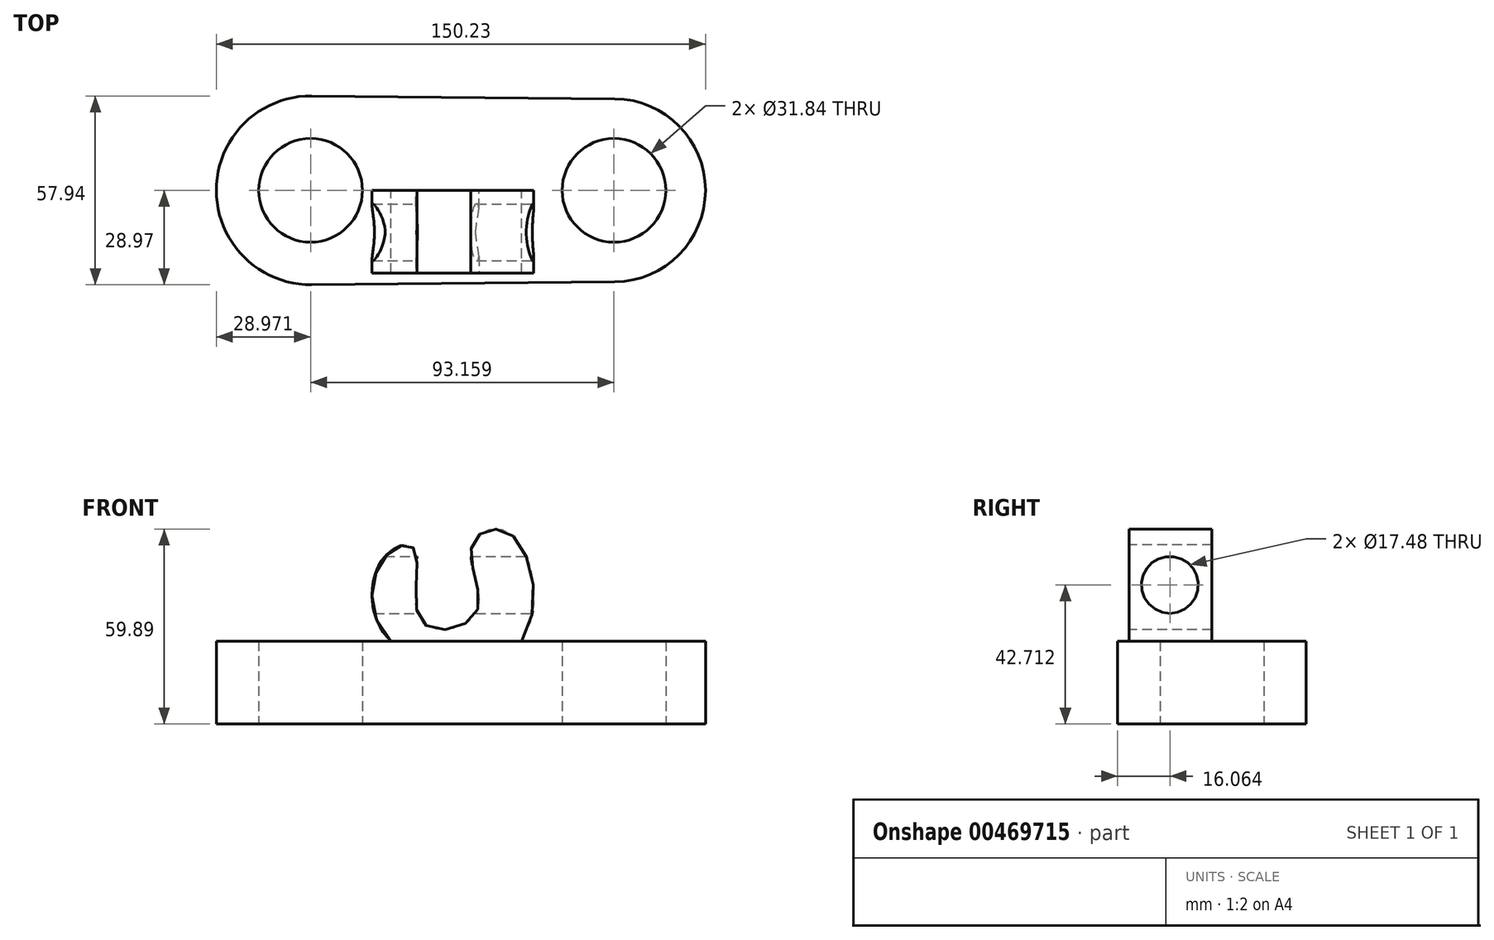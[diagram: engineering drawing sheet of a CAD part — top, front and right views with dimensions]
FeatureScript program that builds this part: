
annotation { "Feature Type Name" : "Feature", "Feature Type Description" : "" }
export const myFeature = defineFeature(function(context is Context, id is Id, definition is map)
    precondition{}
    {
        {
            var Q0;
            Q0=qCreatedBy(makeId("Top.planeOp"),FACE);
            var sketch = newSketch(context, id + "F0", { "sketchPlane" : qUnion([Q0])});
            skCircle(sketch, "E0", {"center": v(-46.58, 0) * mm, "radius": 15.92 * mm});
            skCircle(sketch, "E1", {"center": v(46.58, 0) * mm, "radius": 15.92 * mm});
            skArc(sketch, "E2", {"start": v(-46.3, 28.97) * mm, "mid": v(-75.55, 0) * mm, "end": v(-46.3, -28.97) * mm});
            skArc(sketch, "E3", {"start": v(46.84, -28.1) * mm, "mid": v(74.68, 0) * mm, "end": v(46.84, 28.1) * mm});
            skLineSegment(sketch, "E4", {"start": v(-46.3, 28.97) * mm, "end": v(46.84, 28.1) * mm});
            skLineSegment(sketch, "E5", {"start": v(46.84, -28.1) * mm, "end": v(-46.3, -28.97) * mm});
            skArc(sketch, "E6", {"start": v(-46.3, -28.97) * mm, "mid": v(-17.6, 0) * mm, "end": v(-46.3, 28.97) * mm});
            skSolve(sketch);
        }
        {
            var Q0;
            Q0=makeQuery(id+"F0.imprint","IMPRINT",FACE,{"disambiguationData":[TD([[makeQuery(id+"F0.imprint","IMPRINT",EDGE,{"derivedFrom":sQuery(id+"F0.wireOp",EDGE,"E0")}),-1.0]])]});
            extrude(context, id + "F1", {"entities" : qUnion([Q0]), "depth" : 25.4 * mm});
        }
        {
            var Q0;
            Q0=makeQuery(id+"F0.imprint","IMPRINT",FACE,{"disambiguationData":[TD([[makeQuery(id+"F0.imprint","IMPRINT",EDGE,{"derivedFrom":sQuery(id+"F0.wireOp",EDGE,"E1")}),-1.0]])]});
            extrude(context, id + "F2", {"entities" : qUnion([Q0]), "operationType" : NewBodyOperationType.ADD, "depth" : 25.4 * mm});
        }
        {
            var Q0;
            {var subQ0=sQuery(id+"F0.wireOp",EDGE,"E6");Q0=makeQuery(id+"F2.boolean.opBoolean","MERGE",FACE,{"derivedFrom":[makeQuery(id+"F1.opExtrude","CAP_FACE",FACE,{"disambiguationData":[OSD([sQuery(id+"F0.wireOp",EDGE,"E0"),sQuery(id+"F0.wireOp",EDGE,"E2"),subQ0])],"isStart":false}),makeQuery(id+"F2.opExtrude","CAP_FACE",FACE,{"disambiguationData":[OSD([sQuery(id+"F0.wireOp",EDGE,"E1"),sQuery(id+"F0.wireOp",EDGE,"E3"),sQuery(id+"F0.wireOp",EDGE,"E4"),sQuery(id+"F0.wireOp",EDGE,"E5"),subQ0])],"isStart":false})]});}
            var sketch = newSketch(context, id + "F3", { "sketchPlane" : qUnion([Q0])});
            skLineSegment(sketch, "E7", {"start": v(-21.34, -28.74) * mm, "end": v(-21.34, 28.74) * mm});
            skLineSegment(sketch, "E8", {"start": v(-21.34, 28.74) * mm, "end": v(18.65, 28.37) * mm});
            skLineSegment(sketch, "E9", {"start": v(18.65, 28.37) * mm, "end": v(19.19, -28.97) * mm});
            skLineSegment(sketch, "E10", {"start": v(19.19, -28.97) * mm, "end": v(-21.34, -28.74) * mm});
            skSolve(sketch);
        }
        {
            var Q0;
            {var subQ0=sQuery(id+"F3.wireOp",EDGE,"E7");Q0=makeQuery(id+"F3.imprint","IMPRINT",FACE,{"disambiguationData":[TD([[makeQuery(id+"F3.imprint","IMPRINT",EDGE,{"derivedFrom":subQ0}),-1.0]])]});}
            var sketch = newSketch(context, id + "F4", { "sketchPlane" : qUnion([Q0])});
            skLineSegment(sketch, "E11.bottom", {"start": v(-20.47, -11.1) * mm, "end": v(18.56, -11.1) * mm});
            skLineSegment(sketch, "E11.top", {"start": v(-20.47, 17.87) * mm, "end": v(18.56, 17.87) * mm});
            skLineSegment(sketch, "E11.left", {"start": v(-20.47, -11.1) * mm, "end": v(-20.47, 17.87) * mm});
            skLineSegment(sketch, "E11.right", {"start": v(18.56, -11.1) * mm, "end": v(18.56, 17.87) * mm});
            skSolve(sketch);
        }
        {
            var Q0;
            Q0=qCreatedBy(makeId("Front.planeOp"),FACE);
            var sketch = newSketch(context, id + "F5", { "sketchPlane" : qUnion([Q0])});
            skFitSpline(sketch, "E12", {"points": [v(-23.87, 51.26) * mm, v(-22.35, 25.8) * mm, v(17.25, 24.22) * mm, v(14.58, 58.54) * mm, v(2.96, 54.78) * mm, v(4.2, 34.02) * mm, v(-12.4, 31.33) * mm, v(-14.65, 53.6) * mm, v(-23.87, 51.26) * mm]});
            skSolve(sketch);
        }
        {
            var Q0;
            Q0 = qSketchRegion(id + "F5", true);
            extrude(context, id + "F6", {"entities" : qUnion([Q0]), "operationType" : NewBodyOperationType.ADD, "depth" : 25.4 * mm});
        }
        {
            var Q0;
            Q0=qCreatedBy(makeId("Right.planeOp"),FACE);
            var sketch = newSketch(context, id + "F7", { "sketchPlane" : qUnion([Q0])});
            skCircle(sketch, "E13", {"center": v(-12.9, 42.71) * mm, "radius": 8.74 * mm});
            skSolve(sketch);
        }
        {
            var Q0;
            Q0 = qSketchRegion(id + "F7", true);
            extrude(context, id + "F8", {"entities" : qUnion([Q0]), "operationType" : NewBodyOperationType.REMOVE, "endBound" : BoundingType.SYMMETRIC, "oppositeDirection" : true, "depth" : 104.65 * mm});
        }
    });
